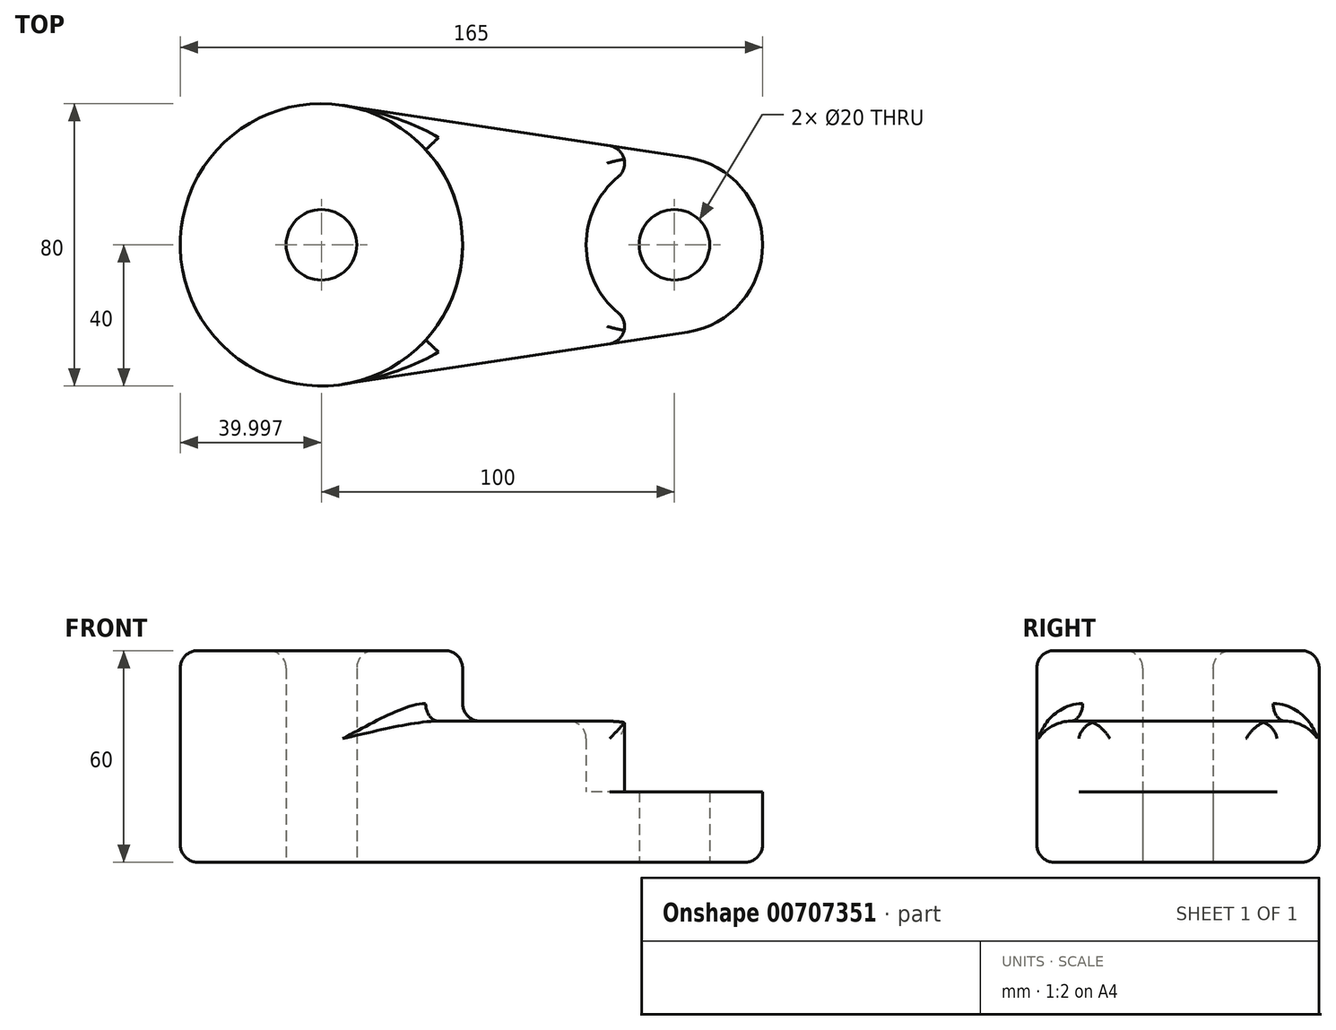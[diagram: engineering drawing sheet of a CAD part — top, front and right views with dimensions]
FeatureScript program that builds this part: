
annotation { "Feature Type Name" : "Feature", "Feature Type Description" : "" }
export const myFeature = defineFeature(function(context is Context, id is Id, definition is map)
    precondition{}
    {
        {
            var Q0;
            Q0=qCreatedBy(makeId("Top.planeOp"),FACE);
            var sketch = newSketch(context, id + "F0", { "sketchPlane" : qUnion([Q0])});
            skCircle(sketch, "E0", {"center": v(48.19, 0) * mm, "radius": 25 * mm});
            skCircle(sketch, "E1", {"center": v(48.19, 0) * mm, "radius": 10 * mm});
            skCircle(sketch, "E2", {"center": v(-51.81, 0) * mm, "radius": 40 * mm});
            skCircle(sketch, "E3", {"center": v(-51.81, 0) * mm, "radius": 10 * mm});
            skLineSegment(sketch, "E4", {"start": v(-45.81, 39.55) * mm, "end": v(51.94, 24.72) * mm});
            skLineSegment(sketch, "E5", {"start": v(-45.81, -39.55) * mm, "end": v(51.94, -24.72) * mm});
            skSolve(sketch);
        }
        {
            var Q0;
            Q0=makeQuery(id+"F0.imprint","IMPRINT",FACE,{"disambiguationData":[TD([[makeQuery(id+"F0.imprint","IMPRINT",EDGE,{"derivedFrom":sQuery(id+"F0.wireOp",EDGE,"E3")}),-1.0]])]});
            extrude(context, id + "F1", {"entities" : qUnion([Q0]), "depth" : 60 * mm, "offsetDistance" : 25 * mm});
        }
        {
            var Q0;
            {var subQ0=sQuery(id+"F0.wireOp",EDGE,"E4");Q0=makeQuery(id+"F0.imprint","IMPRINT",FACE,{"disambiguationData":[TD([[makeQuery(id+"F0.imprint","IMPRINT",EDGE,{"derivedFrom":subQ0}),-1.0]])]});}
            extrude(context, id + "F2", {"entities" : qUnion([Q0]), "operationType" : NewBodyOperationType.ADD, "depth" : 40 * mm, "offsetDistance" : 25 * mm});
        }
        {
            var Q0;
            Q0=makeQuery(id+"F0.imprint","IMPRINT",FACE,{"disambiguationData":[TD([[makeQuery(id+"F0.imprint","IMPRINT",EDGE,{"derivedFrom":sQuery(id+"F0.wireOp",EDGE,"E1")}),-1.0]])]});
            extrude(context, id + "F3", {"entities" : qUnion([Q0]), "operationType" : NewBodyOperationType.ADD, "depth" : 20 * mm, "offsetDistance" : 25 * mm});
        }
        {
            var Q0;
            Q0=makeQuery(id+"F1.opExtrude","CAP_FACE",FACE,{"disambiguationData":[OSD([sQuery(id+"F0.wireOp",EDGE,"E2"),sQuery(id+"F0.wireOp",EDGE,"E3")])],"isStart":false});
            var Q1;
            Q1=makeQuery(id+"F1.opExtrude","SWEPT_FACE",FACE,{"disambiguationData":[OSD([sQuery(id+"F0.wireOp",EDGE,"E2")])]});
            var Q2;
            Q2=makeQuery(id+"F2.opExtrude","CAP_FACE",FACE,{"disambiguationData":[OSD([sQuery(id+"F0.wireOp",EDGE,"E0"),sQuery(id+"F0.wireOp",EDGE,"E2"),sQuery(id+"F0.wireOp",EDGE,"E4"),sQuery(id+"F0.wireOp",EDGE,"E5")])],"isStart":false});
            fillet(context, id + "F4", {"entities" : qUnion([Q0, Q1, Q2]), "radius" : 5 * mm, "tangentPropagation" : true, "allowEdgeOverflow" : false});
        }
        {
            var Q0;
            {var subQ0=sQuery(id+"F0.wireOp",EDGE,"E0");var subQ1=sQuery(id+"F0.wireOp",EDGE,"E5");Q0=makeQuery(id+"F3.boolean.opBoolean","SPLIT",EDGE,{"disambiguationData":[topologyDisambiguationEdgeConnected([makeQuery(id+"F2.opExtrude","SWEPT_FACE",FACE,{"disambiguationData":[OSD([subQ0])]})])],"derivedFrom":makeQuery(id+"F2.opExtrude","SWEPT_EDGE",EDGE,{"disambiguationData":[OSD([subQ0,subQ1])]})});}
            var Q1;
            {var subQ0=sQuery(id+"F0.wireOp",EDGE,"E0");var subQ1=sQuery(id+"F0.wireOp",EDGE,"E4");Q1=makeQuery(id+"F3.boolean.opBoolean","SPLIT",EDGE,{"disambiguationData":[topologyDisambiguationEdgeConnected([makeQuery(id+"F2.opExtrude","SWEPT_FACE",FACE,{"disambiguationData":[OSD([subQ0])]})])],"derivedFrom":makeQuery(id+"F2.opExtrude","SWEPT_EDGE",EDGE,{"disambiguationData":[OSD([subQ0,subQ1])]})});}
            fillet(context, id + "F5", {"entities" : qUnion([Q0, Q1]), "radius" : 5 * mm, "tangentPropagation" : true, "allowEdgeOverflow" : false});
        }
    });
